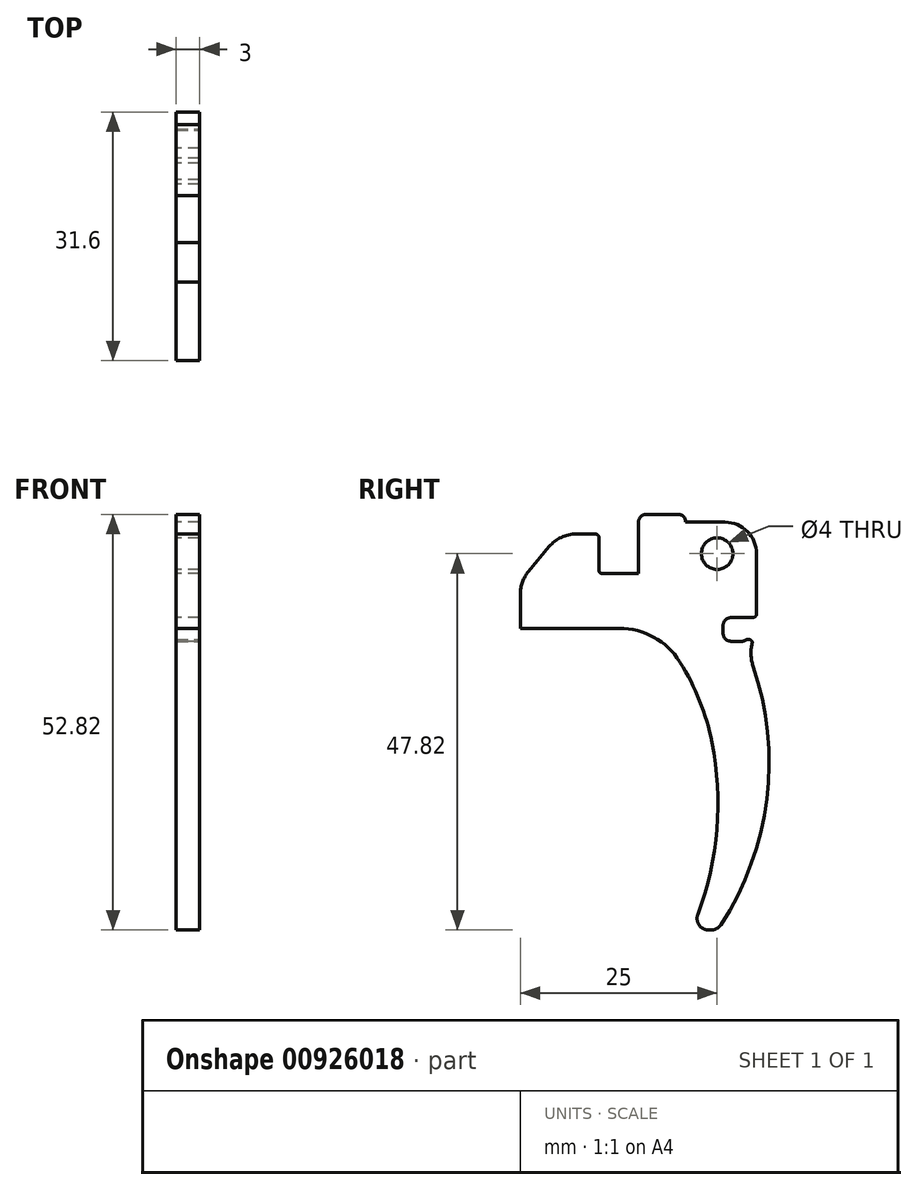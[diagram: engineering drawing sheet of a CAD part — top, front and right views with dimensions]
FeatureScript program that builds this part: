
annotation { "Feature Type Name" : "Feature", "Feature Type Description" : "" }
export const myFeature = defineFeature(function(context is Context, id is Id, definition is map)
    precondition{}
    {
        {
            var Q0;
            Q0=qCreatedBy(makeId("Right.planeOp"),FACE);
            var sketch = newSketch(context, id + "F0", { "sketchPlane" : qUnion([Q0])});
            skCircle(sketch, "E0", {"center": v(0, 0) * mm, "radius": 2 * mm});
            skLineSegment(sketch, "E1", {"start": v(-10, -2.5) * mm, "end": v(-14.7, -2.5) * mm});
            skLineSegment(sketch, "E2", {"start": v(-15, 1.78) * mm, "end": v(-15, -2.2) * mm});
            skLineSegment(sketch, "E3", {"start": v(-25, -9.5) * mm, "end": v(-7.97, -9.5) * mm});
            skPoint(sketch, "E4.orphan", {"position": v(0, -9.5) * mm});
            skPoint(sketch, "E5.visualSharp", {"position": v(-20, -9.5) * mm});
            skPoint(sketch, "E6.visualSharp", {"position": v(-3.5, -9.5) * mm});
            skPoint(sketch, "E7.visualSharp", {"position": v(-4, -2.5) * mm});
            skPoint(sketch, "E8.visualSharp", {"position": v(-15, 2.5) * mm});
            skPoint(sketch, "E9.visualSharp", {"position": v(-15, -2.5) * mm});
            skArc(sketch, "E9.filletArc", {"start": v(-15, -2.2) * mm, "mid": v(-14.91, -2.41) * mm, "end": v(-14.7, -2.5) * mm});
            skArc(sketch, "E10", {"start": v(-25, -9.43) * mm, "mid": v(-25, -9.47) * mm, "end": v(-25, -9.5) * mm});
            skLineSegment(sketch, "E11", {"start": v(-7.12, -9.97) * mm, "end": v(-2.75, -16.92) * mm});
            skLineSegment(sketch, "E12.bottom", {"start": v(3.28, -8.13) * mm, "end": v(1.76, -8.13) * mm});
            skLineSegment(sketch, "E12.top", {"start": v(3.06, -11.13) * mm, "end": v(1.76, -11.13) * mm});
            skLineSegment(sketch, "E12.right", {"start": v(0.76, -9.13) * mm, "end": v(0.76, -10.13) * mm});
            skPoint(sketch, "E13.visualSharp", {"position": v(0.76, -8.13) * mm});
            skArc(sketch, "E13.filletArc", {"start": v(1.76, -8.13) * mm, "mid": v(1.05, -8.42) * mm, "end": v(0.76, -9.13) * mm});
            skPoint(sketch, "E14.visualSharp", {"position": v(0.76, -11.13) * mm});
            skArc(sketch, "E14.filletArc", {"start": v(0.76, -10.13) * mm, "mid": v(1.05, -10.84) * mm, "end": v(1.76, -11.13) * mm});
            skPoint(sketch, "E15.visualSharp", {"position": v(3.76, -8.13) * mm});
            skLineSegment(sketch, "E16.bottom", {"start": v(-15, 2.5) * mm, "end": v(-20, 2.5) * mm});
            skLineSegment(sketch, "E16.top", {"start": v(-15, -9.5) * mm, "end": v(-25, -9.5) * mm});
            skLineSegment(sketch, "E16.left", {"start": v(-15, 2.5) * mm, "end": v(-15, -9.5) * mm});
            skLineSegment(sketch, "E16.right", {"start": v(-25, -3.5) * mm, "end": v(-25, -9.5) * mm});
            skLineSegment(sketch, "E17", {"start": v(-20, 2.5) * mm, "end": v(-25, -3.5) * mm});
            skPoint(sketch, "E18.orphan", {"position": v(-25, 2.5) * mm});
            skPoint(sketch, "E19.endSnap0", {"position": v(-9.85, -2.5) * mm});
            skLineSegment(sketch, "E20", {"start": v(-10, -2.5) * mm, "end": v(-10, 5) * mm});
            skLineSegment(sketch, "E21", {"start": v(-10, 5) * mm, "end": v(-4, 5) * mm});
            skPoint(sketch, "E21.endSnap0", {"position": v(0, 4) * mm});
            skLineSegment(sketch, "E22", {"start": v(-4, 4) * mm, "end": v(-4, 5) * mm});
            skLineSegment(sketch, "E23", {"start": v(0, 4) * mm, "end": v(-4, 4) * mm});
            skPoint(sketch, "E24.orphan", {"position": v(0, 5) * mm});
            skPoint(sketch, "E25.orphan", {"position": v(-5, -2.5) * mm});
            skPoint(sketch, "E26.orphan", {"position": v(-4, 0) * mm});
            skLineSegment(sketch, "E27", {"start": v(-3.28, -47.82) * mm, "end": v(0, -47.82) * mm});
            skArc(sketch, "E28", {"start": v(0, -47.82) * mm, "mid": v(6.42, -30.2) * mm, "end": v(3.56, -11.66) * mm});
            skArc(sketch, "E29", {"start": v(-3.28, -47.82) * mm, "mid": v(0.1, -32.42) * mm, "end": v(-2.75, -16.92) * mm});
            skLineSegment(sketch, "E30", {"start": v(-7.97, -9.5) * mm, "end": v(-7.43, -9.5) * mm});
            skLineSegment(sketch, "E31", {"start": v(-7.12, -9.97) * mm, "end": v(-7.43, -9.5) * mm});
            skLineSegment(sketch, "E32", {"start": v(3.06, -11.13) * mm, "end": v(3.33, -11.13) * mm});
            skLineSegment(sketch, "E33", {"start": v(3.56, -11.66) * mm, "end": v(3.33, -11.13) * mm});
            skLineSegment(sketch, "E34", {"start": v(0, 4) * mm, "end": v(4, 4) * mm});
            skLineSegment(sketch, "E35", {"start": v(3.28, -8.13) * mm, "end": v(4, -8.13) * mm});
            skLineSegment(sketch, "E36.bottom", {"start": v(4, 4) * mm, "end": v(5, 4) * mm});
            skLineSegment(sketch, "E36.top", {"start": v(4, -8.13) * mm, "end": v(5, -8.13) * mm});
            skLineSegment(sketch, "E36.right", {"start": v(5, 4) * mm, "end": v(5, -8.13) * mm});
            skPoint(sketch, "E37.start.orphan", {"position": v(4, 0) * mm});
            skSolve(sketch);
        }
        {
            var Q0;
            Q0=qSketchRegion(id+"F0",true);
            extrude(context, id + "F1", {"entities" : qUnion([Q0]), "depth" : 3 * mm, "offsetDistance" : 25 * mm});
        }
        {
            var Q0;
            Q0=makeQuery(id+"F1.opExtrude","SWEPT_EDGE",EDGE,{"disambiguationData":[OSD([sQuery(id+"F0.wireOp",EDGE,"E16.bottom"),sQuery(id+"F0.wireOp",EDGE,"E17")])]});
            var Q1;
            Q1=makeQuery(id+"F1.opExtrude","SWEPT_EDGE",EDGE,{"disambiguationData":[OSD([sQuery(id+"F0.wireOp",EDGE,"E16.right"),sQuery(id+"F0.wireOp",EDGE,"E17")])]});
            var Q2;
            Q2=makeQuery(id+"F1.opExtrude","SWEPT_EDGE",EDGE,{"disambiguationData":[OSD([sQuery(id+"F0.wireOp",EDGE,"E16.top"),sQuery(id+"F0.wireOp",EDGE,"E16.right")])]});
            fillet(context, id + "F2", {"entities" : qUnion([Q0, Q1, Q2]), "radius" : 4.5 * mm, "tangentPropagation" : true, "allowEdgeOverflow" : false});
        }
        {
            var Q0;
            Q0=makeQuery(id+"F1.opExtrude","SWEPT_EDGE",EDGE,{"disambiguationData":[OSD([sQuery(id+"F0.wireOp",EDGE,"E16.bottom"),sQuery(id+"F0.wireOp",EDGE,"E16.left")])]});
            fillet(context, id + "F3", {"entities" : qUnion([Q0]), "radius" : 0.5 * mm, "tangentPropagation" : true, "allowEdgeOverflow" : false});
        }
        {
            var Q0;
            Q0=makeQuery(id+"F1.opExtrude","SWEPT_EDGE",EDGE,{"disambiguationData":[OSD([sQuery(id+"F0.wireOp",EDGE,"E20"),sQuery(id+"F0.wireOp",EDGE,"E21")])]});
            var Q1;
            Q1=makeQuery(id+"F1.opExtrude","SWEPT_EDGE",EDGE,{"disambiguationData":[OSD([sQuery(id+"F0.wireOp",EDGE,"E21"),sQuery(id+"F0.wireOp",EDGE,"E22")])]});
            fillet(context, id + "F4", {"entities" : qUnion([Q0, Q1]), "radius" : 1 * mm, "tangentPropagation" : true, "allowEdgeOverflow" : false});
        }
        {
            var Q0;
            Q0=makeQuery(id+"F1.opExtrude","SWEPT_EDGE",EDGE,{"disambiguationData":[OSD([sQuery(id+"F0.wireOp",EDGE,"E27"),sQuery(id+"F0.wireOp",EDGE,"E29")])]});
            var Q1;
            Q1=makeQuery(id+"F1.opExtrude","SWEPT_EDGE",EDGE,{"disambiguationData":[OSD([sQuery(id+"F0.wireOp",EDGE,"E27"),sQuery(id+"F0.wireOp",EDGE,"E28")])]});
            fillet(context, id + "F5", {"entities" : qUnion([Q0, Q1]), "radius" : 1.5 * mm, "tangentPropagation" : true, "allowEdgeOverflow" : false});
        }
        {
            var Q0;
            Q0=makeQuery(id+"F1.opExtrude","SWEPT_EDGE",EDGE,{"disambiguationData":[OSD([sQuery(id+"F0.wireOp",EDGE,"E11"),sQuery(id+"F0.wireOp",EDGE,"E29")])]});
            fillet(context, id + "F6", {"entities" : qUnion([Q0]), "radius" : 30 * mm, "tangentPropagation" : true, "allowEdgeOverflow" : false});
        }
        {
            var Q0;
            Q0=makeQuery(id+"F1.opExtrude","SWEPT_EDGE",EDGE,{"disambiguationData":[OSD([sQuery(id+"F0.wireOp",EDGE,"E30"),sQuery(id+"F0.wireOp",EDGE,"E31")])]});
            fillet(context, id + "F7", {"entities" : qUnion([Q0]), "radius" : 9 * mm, "tangentPropagation" : true, "allowEdgeOverflow" : false});
        }
        {
            var Q0;
            Q0=makeQuery(id+"F1.opExtrude","SWEPT_FACE",FACE,{"disambiguationData":[OSD([sQuery(id+"F0.wireOp",EDGE,"E33")])]});
            extrude(context, id + "F8", {"entities" : qUnion([Q0]), "operationType" : NewBodyOperationType.ADD, "depth" : 1 * mm, "offsetDistance" : 25 * mm});
        }
        {
            var Q0;
            {var subQ0=sQuery(id+"F0.wireOp",EDGE,"E33");var subQ1=sQuery(id+"F0.wireOp",EDGE,"E28");Q0=makeQuery(id+"F8.boolean.opBoolean","MERGE",EDGE,{"derivedFrom":[makeQuery(id+"F1.opExtrude","SWEPT_EDGE",EDGE,{"disambiguationData":[OSD([subQ1,subQ0])]}),makeQuery(id+"F8.opExtrude","CAP_EDGE",EDGE,{"disambiguationData":[OSD([subQ1,subQ0])],"isStart":true})]});}
            fillet(context, id + "F9", {"entities" : qUnion([Q0]), "radius" : 5 * mm, "tangentPropagation" : true, "allowEdgeOverflow" : false});
        }
        {
            var Q0;
            Q0=makeQuery(id+"F8.opExtrude","CAP_EDGE",EDGE,{"disambiguationData":[OSD([sQuery(id+"F0.wireOp",EDGE,"E32"),sQuery(id+"F0.wireOp",EDGE,"E33")])],"isStart":false});
            var Q1;
            {var subQ0=sQuery(id+"F0.wireOp",EDGE,"E33");var subQ1=sQuery(id+"F0.wireOp",EDGE,"E28");Q1=makeQuery(id+"F9.opFillet","BLEND_EDGE",EDGE,{"blendedFrom":[makeQuery(id+"F8.boolean.opBoolean","MERGE",EDGE,{"derivedFrom":[makeQuery(id+"F1.opExtrude","SWEPT_EDGE",EDGE,{"disambiguationData":[OSD([subQ1,subQ0])]}),makeQuery(id+"F8.opExtrude","CAP_EDGE",EDGE,{"disambiguationData":[OSD([subQ1,subQ0])],"isStart":true})]}),makeQuery(id+"F8.opExtrude","CAP_FACE",FACE,{"disambiguationData":[OSD([subQ0])],"isStart":false})],"blendedInto":[makeQuery(id+"F8.opExtrude","CAP_FACE",FACE,{"disambiguationData":[OSD([subQ0])],"isStart":false})]});}
            var Q2;
            {var subQ0=sQuery(id+"F0.wireOp",EDGE,"E33");var subQ1=sQuery(id+"F0.wireOp",EDGE,"E32");Q2=makeQuery(id+"F8.boolean.opBoolean","MERGE",EDGE,{"derivedFrom":[makeQuery(id+"F1.opExtrude","SWEPT_EDGE",EDGE,{"disambiguationData":[OSD([subQ1,subQ0])]}),makeQuery(id+"F8.opExtrude","CAP_EDGE",EDGE,{"disambiguationData":[OSD([subQ1,subQ0])],"isStart":true})]});}
            var Q3;
            Q3=makeQuery(id+"F1.opExtrude","SWEPT_EDGE",EDGE,{"disambiguationData":[OSD([sQuery(id+"F0.wireOp",EDGE,"E12.top"),sQuery(id+"F0.wireOp",EDGE,"E14.filletArc")])]});
            fillet(context, id + "F10", {"entities" : qUnion([Q0, Q1, Q2, Q3]), "radius" : .5 * mm, "tangentPropagation" : true, "allowEdgeOverflow" : false});
        }
        {
            var Q0;
            Q0=makeQuery(id+"F1.opExtrude","SWEPT_EDGE",EDGE,{"disambiguationData":[OSD([sQuery(id+"F0.wireOp",EDGE,"E36.top"),sQuery(id+"F0.wireOp",EDGE,"E36.right")])]});
            fillet(context, id + "F11", {"entities" : qUnion([Q0]), "radius" : .5 * mm, "tangentPropagation" : true, "allowEdgeOverflow" : false});
        }
        {
            var Q0;
            Q0=makeQuery(id+"F1.opExtrude","SWEPT_EDGE",EDGE,{"disambiguationData":[OSD([sQuery(id+"F0.wireOp",EDGE,"E36.bottom"),sQuery(id+"F0.wireOp",EDGE,"E36.right")])]});
            fillet(context, id + "F12", {"entities" : qUnion([Q0]), "radius" : 4 * mm, "tangentPropagation" : true, "allowEdgeOverflow" : false});
        }
    });
